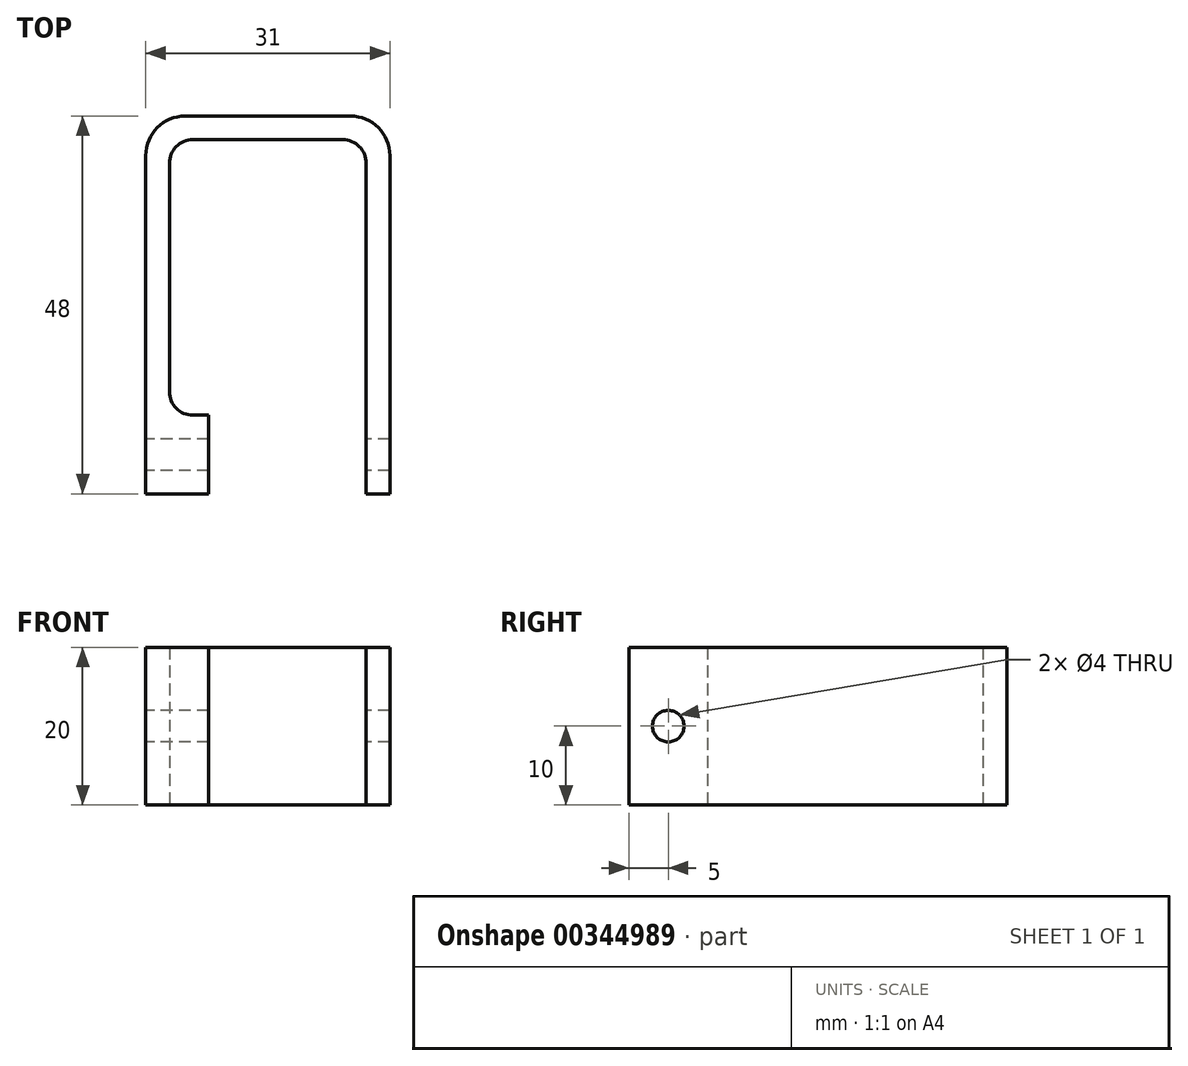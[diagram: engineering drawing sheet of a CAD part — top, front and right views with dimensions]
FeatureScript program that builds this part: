
annotation { "Feature Type Name" : "Feature", "Feature Type Description" : "" }
export const myFeature = defineFeature(function(context is Context, id is Id, definition is map)
    precondition{}
    {
        {
            var Q0;
            Q0=qCreatedBy(makeId("Top.planeOp"),FACE);
            var sketch = newSketch(context, id + "F0", { "sketchPlane" : qUnion([Q0])});
            skLineSegment(sketch, "E0.bottom", {"start": v(-44.08, 0) * mm, "end": v(-19.08, 0) * mm});
            skLineSegment(sketch, "E0.top", {"start": v(-44.08, 25) * mm, "end": v(-19.08, 25) * mm});
            skLineSegment(sketch, "E0.left", {"start": v(-44.08, 0) * mm, "end": v(-44.08, 25) * mm});
            skLineSegment(sketch, "E0.right", {"start": v(-19.08, 0) * mm, "end": v(-19.08, 25) * mm});
            skLineSegment(sketch, "E1.bottom", {"start": v(-44.08, 0) * mm, "end": v(-47.08, 0) * mm});
            skLineSegment(sketch, "E1.top", {"start": v(-44.08, 28) * mm, "end": v(-47.08, 28) * mm});
            skLineSegment(sketch, "E1.left", {"start": v(-44.08, 0) * mm, "end": v(-44.08, 28) * mm});
            skLineSegment(sketch, "E1.right", {"start": v(-47.08, 0) * mm, "end": v(-47.08, 28) * mm});
            skLineSegment(sketch, "E2.bottom", {"start": v(-19.08, 0) * mm, "end": v(-16.08, 0) * mm});
            skLineSegment(sketch, "E2.top", {"start": v(-19.08, 28) * mm, "end": v(-16.08, 28) * mm});
            skLineSegment(sketch, "E2.left", {"start": v(-19.08, 0) * mm, "end": v(-19.08, 28) * mm});
            skLineSegment(sketch, "E2.right", {"start": v(-16.08, 0) * mm, "end": v(-16.08, 28) * mm});
            skLineSegment(sketch, "E3", {"start": v(-44.08, 28) * mm, "end": v(-19.08, 28) * mm});
            skLineSegment(sketch, "E4", {"start": v(-44.08, 0) * mm, "end": v(-44.08, -10) * mm});
            skLineSegment(sketch, "E5", {"start": v(-44.08, -10) * mm, "end": v(-39.08, -10) * mm});
            skLineSegment(sketch, "E6", {"start": v(-39.08, -10) * mm, "end": v(-39.08, -20) * mm});
            skLineSegment(sketch, "E7", {"start": v(-39.08, -20) * mm, "end": v(-47.08, -20) * mm});
            skLineSegment(sketch, "E8", {"start": v(-47.08, -20) * mm, "end": v(-47.08, 0) * mm});
            skLineSegment(sketch, "E9", {"start": v(-19.08, -20) * mm, "end": v(-16.08, -20) * mm});
            skLineSegment(sketch, "E10", {"start": v(-16.08, -20) * mm, "end": v(-16.08, 0) * mm});
            skLineSegment(sketch, "E11", {"start": v(-19.08, -20) * mm, "end": v(-19.08, 0) * mm});
            skSolve(sketch);
        }
        {
            var Q0;
            Q0=makeQuery(id+"F0.imprint","IMPRINT",FACE,{"disambiguationData":[TD([[makeQuery(id+"F0.imprint","IMPRINT",EDGE,{"derivedFrom":sQuery(id+"F0.wireOp",EDGE,"E1.bottom")}),1.0]])]});
            var Q1;
            {var subQ3=sQuery(id+"F0.wireOp",EDGE,"E1.bottom");Q1=makeQuery(id+"F0.imprint","IMPRINT",FACE,{"disambiguationData":[TD([[makeQuery(id+"F0.imprint","IMPRINT",EDGE,{"derivedFrom":subQ3}),-1.0]])]});}
            var Q2;
            {var subQ0=sQuery(id+"F0.wireOp",EDGE,"E0.top");Q2=makeQuery(id+"F0.imprint","IMPRINT",FACE,{"disambiguationData":[TD([[makeQuery(id+"F0.imprint","IMPRINT",EDGE,{"derivedFrom":subQ0}),1.0]])]});}
            var Q3;
            {var subQ3=sQuery(id+"F0.wireOp",EDGE,"E2.bottom");Q3=makeQuery(id+"F0.imprint","IMPRINT",FACE,{"disambiguationData":[TD([[makeQuery(id+"F0.imprint","IMPRINT",EDGE,{"derivedFrom":subQ3}),1.0]])]});}
            var Q4;
            Q4=makeQuery(id+"F0.imprint","IMPRINT",FACE,{"disambiguationData":[TD([[makeQuery(id+"F0.imprint","IMPRINT",EDGE,{"derivedFrom":sQuery(id+"F0.wireOp",EDGE,"E2.bottom")}),-1.0]])]});
            extrude(context, id + "F1", {"entities" : qUnion([Q0, Q1, Q2, Q3, Q4]), "depth" : 20 * mm});
        }
        {
            var Q0;
            Q0=makeQuery(id+"F1.opExtrude","SWEPT_FACE",FACE,{"disambiguationData":[OSD([sQuery(id+"F0.wireOp",EDGE,"E1.right"),sQuery(id+"F0.wireOp",EDGE,"E8")])]});
            var sketch = newSketch(context, id + "F2", { "sketchPlane" : qUnion([Q0])});
            skPoint(sketch, "E12", {"position": v(15, 10) * mm});
            skPoint(sketch, "E12.positionSnap0", {"position": v(20, 10) * mm});
            skSolve(sketch);
        }
        {
            var Q0;
            Q0=sQuery(id+"F2.wireOp",VERTEX,"E12");
            var Q1;
            Q1=makeQuery(id+"F1.opExtrude","SWEPT_BODY",BODY,{"disambiguationData":[OSD([sQuery(id+"F0.wireOp",EDGE,"E0.top"),sQuery(id+"F0.wireOp",EDGE,"E1.top"),sQuery(id+"F0.wireOp",EDGE,"E1.left"),sQuery(id+"F0.wireOp",EDGE,"E1.right"),sQuery(id+"F0.wireOp",EDGE,"E2.top"),sQuery(id+"F0.wireOp",EDGE,"E2.left"),sQuery(id+"F0.wireOp",EDGE,"E2.right"),sQuery(id+"F0.wireOp",EDGE,"E3"),sQuery(id+"F0.wireOp",EDGE,"E4"),sQuery(id+"F0.wireOp",EDGE,"E5"),sQuery(id+"F0.wireOp",EDGE,"E6"),sQuery(id+"F0.wireOp",EDGE,"E7"),sQuery(id+"F0.wireOp",EDGE,"E8"),sQuery(id+"F0.wireOp",EDGE,"E9"),sQuery(id+"F0.wireOp",EDGE,"E10"),sQuery(id+"F0.wireOp",EDGE,"E11")])]});
            hole(context, id + "F3", {"style" : HoleStyle.SIMPLE, "endStyle" : HoleEndStyle.BLIND, "holeDiameter" : 4 * mm, "holeDepth" : 120 * mm, "isTappedThrough" : true, "tappedDepth" : 12 * mm, "tapClearance" : 3, "locations" : qUnion([Q0]), "scope" : qUnion([Q1])});
        }
        {
            var Q0;
            Q0=makeQuery(id+"F1.opExtrude","SWEPT_EDGE",EDGE,{"disambiguationData":[OSD([sQuery(id+"F0.wireOp",EDGE,"E0.top"),sQuery(id+"F0.wireOp",EDGE,"E2.left")])]});
            var Q1;
            Q1=makeQuery(id+"F1.opExtrude","SWEPT_EDGE",EDGE,{"disambiguationData":[OSD([sQuery(id+"F0.wireOp",EDGE,"E0.top"),sQuery(id+"F0.wireOp",EDGE,"E1.left")])]});
            var Q2;
            Q2=makeQuery(id+"F1.opExtrude","SWEPT_EDGE",EDGE,{"disambiguationData":[OSD([sQuery(id+"F0.wireOp",EDGE,"E4"),sQuery(id+"F0.wireOp",EDGE,"E5")])]});
            fillet(context, id + "F4", {"entities" : qUnion([Q0, Q1, Q2]), "radius" : 3 * mm, "tangentPropagation" : true, "allowEdgeOverflow" : false});
        }
        {
            var Q0;
            Q0=makeQuery(id+"F1.opExtrude","SWEPT_EDGE",EDGE,{"disambiguationData":[OSD([sQuery(id+"F0.wireOp",EDGE,"E1.top"),sQuery(id+"F0.wireOp",EDGE,"E1.right")])]});
            var Q1;
            Q1=makeQuery(id+"F1.opExtrude","SWEPT_EDGE",EDGE,{"disambiguationData":[OSD([sQuery(id+"F0.wireOp",EDGE,"E2.top"),sQuery(id+"F0.wireOp",EDGE,"E2.right")])]});
            fillet(context, id + "F5", {"entities" : qUnion([Q0, Q1]), "radius" : 5 * mm, "tangentPropagation" : true, "allowEdgeOverflow" : false});
        }
    });
